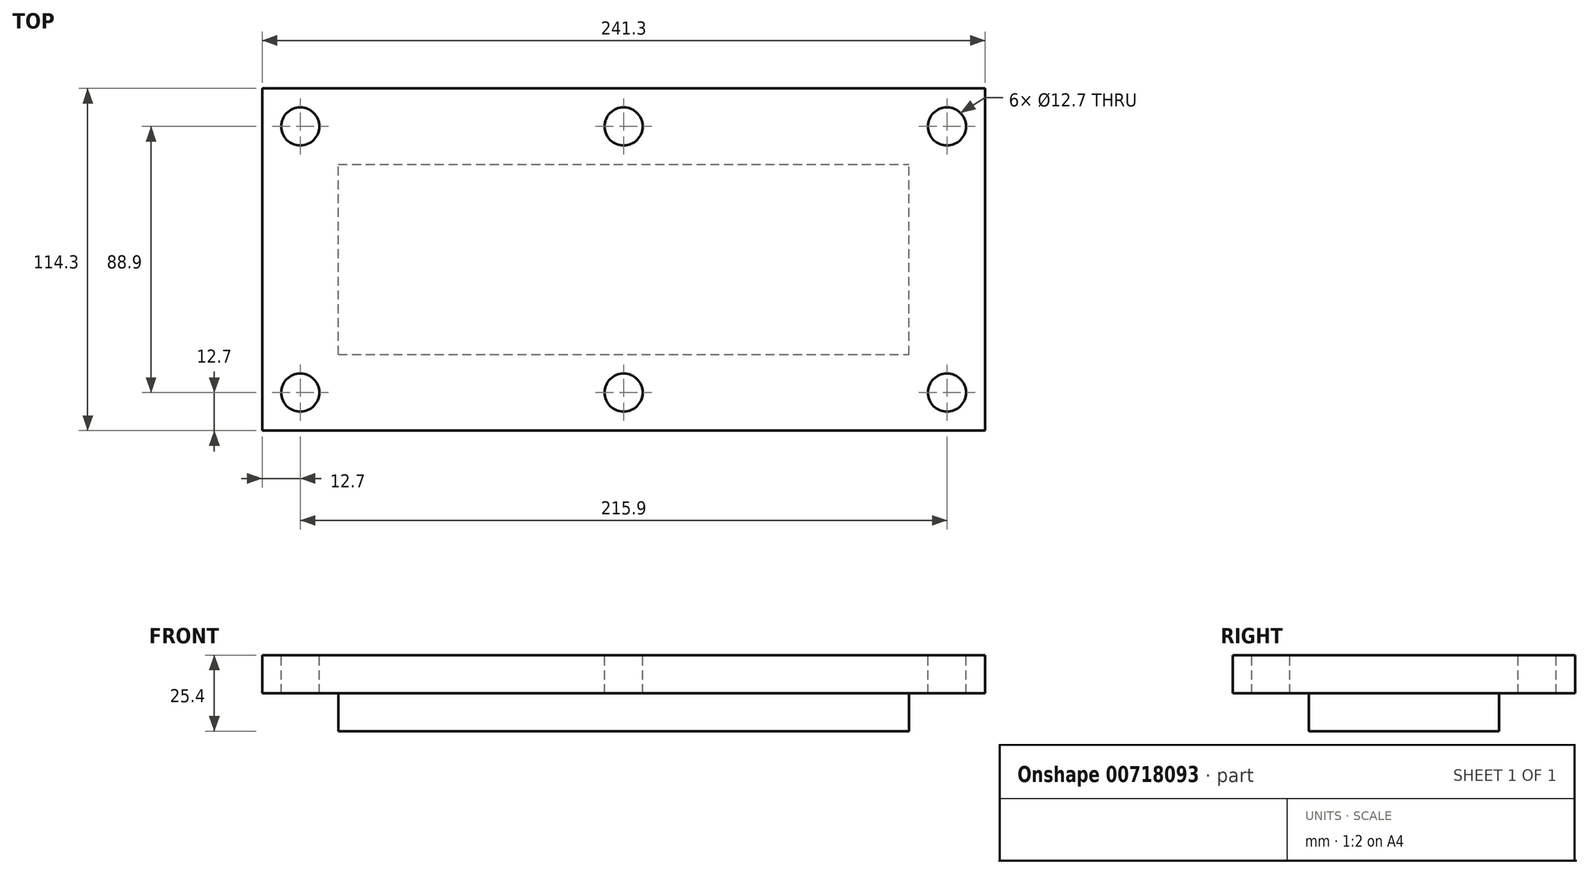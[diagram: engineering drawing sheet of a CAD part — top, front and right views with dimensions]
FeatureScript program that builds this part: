
annotation { "Feature Type Name" : "Feature", "Feature Type Description" : "" }
export const myFeature = defineFeature(function(context is Context, id is Id, definition is map)
    precondition{}
    {
        {
            var Q0;
            Q0=qCreatedBy(makeId("Top.planeOp"),FACE);
            var sketch = newSketch(context, id + "F0", { "sketchPlane" : qUnion([Q0])});
            skLineSegment(sketch, "E0.bottom", {"start": v(120.65, -57.15) * mm, "end": v(-120.65, -57.15) * mm});
            skLineSegment(sketch, "E0.top", {"start": v(120.65, 57.15) * mm, "end": v(-120.65, 57.15) * mm});
            skLineSegment(sketch, "E0.left", {"start": v(120.65, -57.15) * mm, "end": v(120.65, 57.15) * mm});
            skLineSegment(sketch, "E0.right", {"start": v(-120.65, -57.15) * mm, "end": v(-120.65, 57.15) * mm});
            skPoint(sketch, "E0.middle", {"position": v(0, 0) * mm});
            skSolve(sketch);
        }
        {
            var Q0;
            Q0=makeQuery(id+"F0.imprint","IMPRINT",FACE,{"disambiguationData":[TD([[makeQuery(id+"F0.imprint","IMPRINT",EDGE,{"derivedFrom":sQuery(id+"F0.wireOp",EDGE,"A9SU1oPe-u2NT-Cv59-yBqe-lhJK560VMC6y.bottom")}),-1.0]])]});
            var Q1;
            Q1=makeQuery(id+"F0.imprint","IMPRINT",FACE,{"disambiguationData":[TD([[makeQuery(id+"F0.imprint","IMPRINT",EDGE,{"derivedFrom":sQuery(id+"F0.wireOp",EDGE,"E0.bottom")}),-1.0]])]});
            extrude(context, id + "F1", {"entities" : qUnion([Q0, Q1]), "depth" : 12.7 * mm, "offsetDistance" : 25.4 * mm});
        }
        {
            var Q0;
            Q0=makeQuery(id+"F1.opExtrude","CAP_FACE",FACE,{"disambiguationData":[OSD([sQuery(id+"F0.wireOp",EDGE,"E0.bottom"),sQuery(id+"F0.wireOp",EDGE,"E0.top"),sQuery(id+"F0.wireOp",EDGE,"E0.left"),sQuery(id+"F0.wireOp",EDGE,"E0.right")])],"isStart":true});
            var sketch = newSketch(context, id + "F2", { "sketchPlane" : qUnion([Q0])});
            skLineSegment(sketch, "E1.bottom", {"start": v(-95.25, 31.75) * mm, "end": v(95.25, 31.75) * mm});
            skLineSegment(sketch, "E1.top", {"start": v(-95.25, -31.75) * mm, "end": v(95.25, -31.75) * mm});
            skLineSegment(sketch, "E1.left", {"start": v(-95.25, 31.75) * mm, "end": v(-95.25, -31.75) * mm});
            skLineSegment(sketch, "E1.right", {"start": v(95.25, 31.75) * mm, "end": v(95.25, -31.75) * mm});
            skPoint(sketch, "E1.middle", {"position": v(0, 0) * mm});
            skSolve(sketch);
        }
        {
            var Q0;
            Q0=makeQuery(id+"F2.imprint","IMPRINT",FACE,{"disambiguationData":[TD([[makeQuery(id+"F2.imprint","IMPRINT",EDGE,{"derivedFrom":sQuery(id+"F2.wireOp",EDGE,"E1.bottom")}),-1.0]])]});
            extrude(context, id + "F3", {"entities" : qUnion([Q0]), "operationType" : NewBodyOperationType.ADD, "depth" : 12.7 * mm, "offsetDistance" : 25.4 * mm});
        }
        {
            var Q0;
            Q0=makeQuery(id+"F1.opExtrude","CAP_FACE",FACE,{"disambiguationData":[OSD([sQuery(id+"F0.wireOp",EDGE,"E0.bottom"),sQuery(id+"F0.wireOp",EDGE,"E0.top"),sQuery(id+"F0.wireOp",EDGE,"E0.left"),sQuery(id+"F0.wireOp",EDGE,"E0.right")])],"isStart":false});
            var sketch = newSketch(context, id + "F4", { "sketchPlane" : qUnion([Q0])});
            skPoint(sketch, "E2.middle", {"position": v(0, 0) * mm});
            skCircle(sketch, "E3", {"center": v(-107.95, 44.45) * mm, "radius": 6.35 * mm});
            skCircle(sketch, "E4", {"center": v(-107.95, -44.45) * mm, "radius": 6.35 * mm});
            skCircle(sketch, "E5", {"center": v(107.95, -44.45) * mm, "radius": 6.35 * mm});
            skCircle(sketch, "E6", {"center": v(107.95, 44.45) * mm, "radius": 6.35 * mm});
            skCircle(sketch, "E7", {"center": v(0, 44.45) * mm, "radius": 6.35 * mm});
            skCircle(sketch, "E8", {"center": v(0, -44.45) * mm, "radius": 6.35 * mm});
            skSolve(sketch);
        }
        {
            var Q0;
            Q0=makeQuery(id+"F4.imprint","IMPRINT",FACE,{"disambiguationData":[TD([[makeQuery(id+"F4.imprint","IMPRINT",EDGE,{"derivedFrom":sQuery(id+"F4.wireOp",EDGE,"E3")}),1.0]])]});
            var Q1;
            Q1=makeQuery(id+"F4.imprint","IMPRINT",FACE,{"disambiguationData":[TD([[makeQuery(id+"F4.imprint","IMPRINT",EDGE,{"derivedFrom":sQuery(id+"F4.wireOp",EDGE,"E4")}),1.0]])]});
            var Q2;
            Q2=makeQuery(id+"F4.imprint","IMPRINT",FACE,{"disambiguationData":[TD([[makeQuery(id+"F4.imprint","IMPRINT",EDGE,{"derivedFrom":sQuery(id+"F4.wireOp",EDGE,"E5")}),1.0]])]});
            var Q3;
            Q3=makeQuery(id+"F4.imprint","IMPRINT",FACE,{"disambiguationData":[TD([[makeQuery(id+"F4.imprint","IMPRINT",EDGE,{"derivedFrom":sQuery(id+"F4.wireOp",EDGE,"E6")}),1.0]])]});
            var Q4;
            Q4=makeQuery(id+"F4.imprint","IMPRINT",FACE,{"disambiguationData":[TD([[makeQuery(id+"F4.imprint","IMPRINT",EDGE,{"derivedFrom":sQuery(id+"F4.wireOp",EDGE,"E7")}),1.0]])]});
            var Q5;
            Q5=makeQuery(id+"F4.imprint","IMPRINT",FACE,{"disambiguationData":[TD([[makeQuery(id+"F4.imprint","IMPRINT",EDGE,{"derivedFrom":sQuery(id+"F4.wireOp",EDGE,"E8")}),1.0]])]});
            extrude(context, id + "F5", {"entities" : qUnion([Q0, Q1, Q2, Q3, Q4, Q5]), "operationType" : NewBodyOperationType.REMOVE, "oppositeDirection" : true, "depth" : 12.7 * mm, "offsetDistance" : 25.4 * mm});
        }
    });
